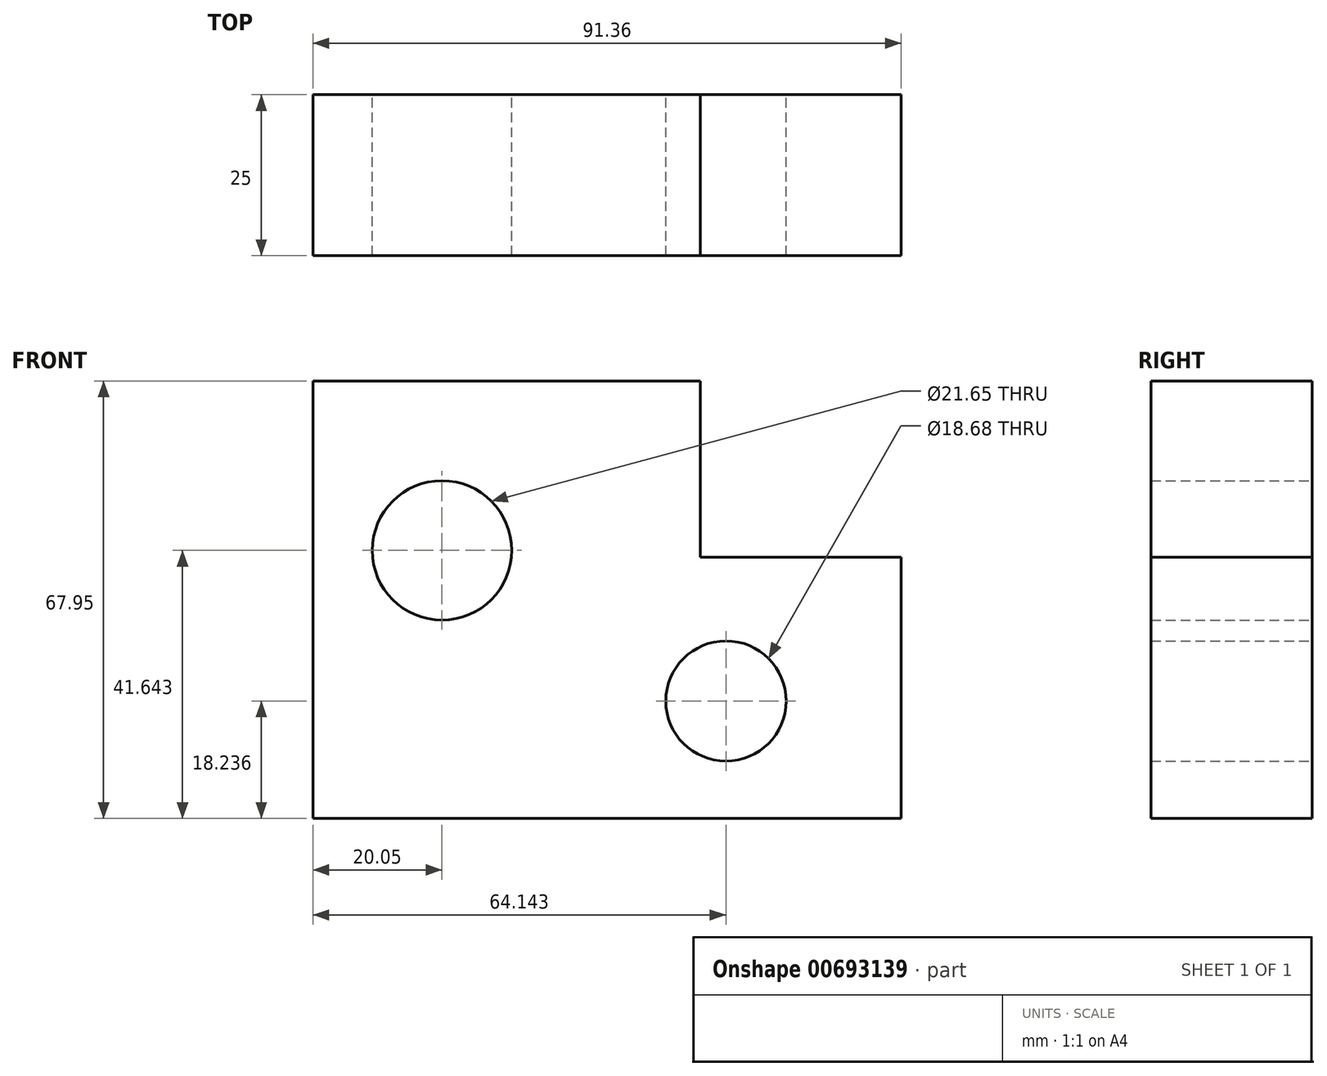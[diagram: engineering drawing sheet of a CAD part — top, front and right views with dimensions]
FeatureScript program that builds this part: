
annotation { "Feature Type Name" : "Feature", "Feature Type Description" : "" }
export const myFeature = defineFeature(function(context is Context, id is Id, definition is map)
    precondition{}
    {
        {
            var Q0;
            Q0=qCreatedBy(makeId("Front.planeOp"),FACE);
            var sketch = newSketch(context, id + "F0", { "sketchPlane" : qUnion([Q0])});
            skLineSegment(sketch, "E0", {"start": v(0, 0) * mm, "end": v(0, 67.95) * mm});
            skLineSegment(sketch, "E1", {"start": v(0, 67.95) * mm, "end": v(60.15, 67.95) * mm});
            skLineSegment(sketch, "E2", {"start": v(60.15, 67.95) * mm, "end": v(60.15, 40.55) * mm});
            skLineSegment(sketch, "E3", {"start": v(60.15, 40.55) * mm, "end": v(91.36, 40.55) * mm});
            skLineSegment(sketch, "E4", {"start": v(91.36, 40.55) * mm, "end": v(91.36, 0) * mm});
            skLineSegment(sketch, "E5", {"start": v(91.36, 0) * mm, "end": v(0, 0) * mm});
            skCircle(sketch, "E6", {"center": v(20.05, 41.64) * mm, "radius": 10.83 * mm});
            skCircle(sketch, "E7", {"center": v(64.14, 18.24) * mm, "radius": 9.34 * mm});
            skSolve(sketch);
        }
        {
            var Q0;
            Q0 = qSketchRegion(id + "F0", true);
            extrude(context, id + "F1", {"entities" : qUnion([Q0]), "depth" : 25 * mm, "offsetDistance" : 25 * mm});
        }
    });
